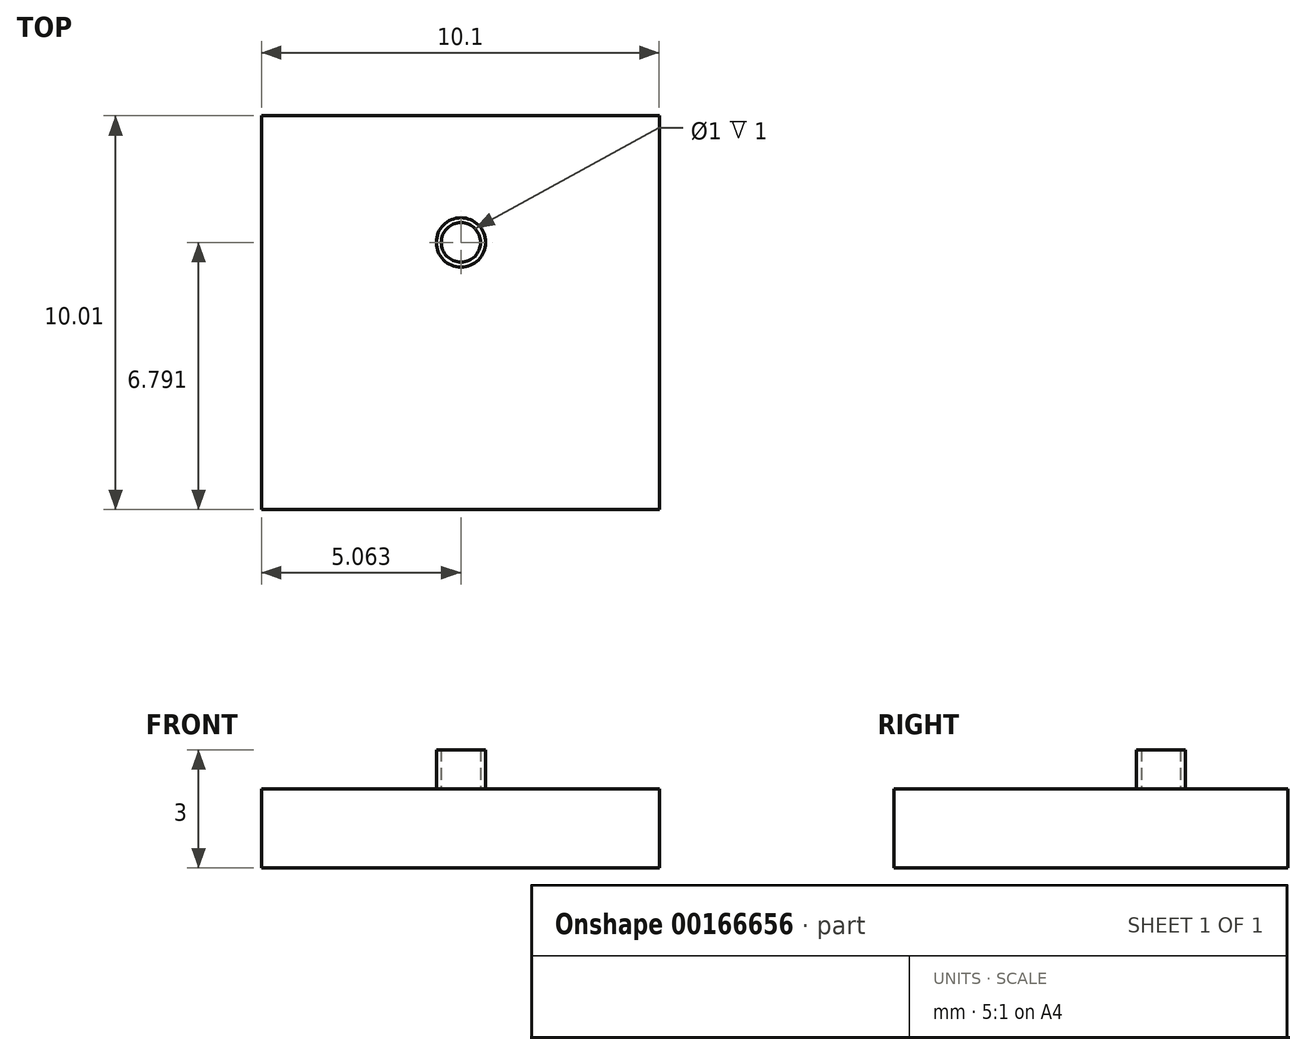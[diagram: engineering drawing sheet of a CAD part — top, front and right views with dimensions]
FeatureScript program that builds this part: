
annotation { "Feature Type Name" : "Feature", "Feature Type Description" : "" }
export const myFeature = defineFeature(function(context is Context, id is Id, definition is map)
    precondition{}
    {
        {
            var Q0;
            Q0=qCreatedBy(makeId("Top.planeOp"),FACE);
            var sketch = newSketch(context, id + "F0", { "sketchPlane" : qUnion([Q0])});
            skLineSegment(sketch, "E0.bottom", {"start": v(0, 0) * mm, "end": v(10.1, 0) * mm});
            skLineSegment(sketch, "E0.top", {"start": v(0, -10) * mm, "end": v(10.1, -10) * mm});
            skLineSegment(sketch, "E0.left", {"start": v(0, 0) * mm, "end": v(0, -10) * mm});
            skLineSegment(sketch, "E0.right", {"start": v(10.1, 0) * mm, "end": v(10.1, -10) * mm});
            skSolve(sketch);
        }
        {
            var Q0;
            Q0=makeQuery(id+"F0.imprint","IMPRINT",FACE,{"disambiguationData":[TD([[makeQuery(id+"F0.imprint","IMPRINT",EDGE,{"derivedFrom":sQuery(id+"F0.wireOp",EDGE,"E0.bottom")}),-1.0]])]});
            extrude(context, id + "F1", {"entities" : qUnion([Q0]), "depth" : 2 * mm});
        }
        {
            var Q0;
            Q0=makeQuery(id+"F1.opExtrude","CAP_FACE",FACE,{"disambiguationData":[OSD([sQuery(id+"F0.wireOp",EDGE,"E0.bottom"),sQuery(id+"F0.wireOp",EDGE,"E0.top"),sQuery(id+"F0.wireOp",EDGE,"E0.left"),sQuery(id+"F0.wireOp",EDGE,"E0.right")])],"isStart":false});
            var sketch = newSketch(context, id + "F2", { "sketchPlane" : qUnion([Q0])});
            skPoint(sketch, "E1", {"position": v(5.06, -3.22) * mm});
            skCircle(sketch, "E2", {"center": v(5.06, -3.22) * mm, "radius": 0.5 * mm});
            skCircle(sketch, "E3", {"center": v(5.06, -3.22) * mm, "radius": 0.63 * mm});
            skSolve(sketch);
        }
        {
            var Q0;
            Q0=makeQuery(id+"F2.imprint","IMPRINT",FACE,{"disambiguationData":[TD([[makeQuery(id+"F2.imprint","IMPRINT",EDGE,{"derivedFrom":sQuery(id+"F2.wireOp",EDGE,"E2")}),-1.0]])]});
            extrude(context, id + "F3", {"entities" : qUnion([Q0]), "operationType" : NewBodyOperationType.ADD, "depth" : 1 * mm});
        }
    });
